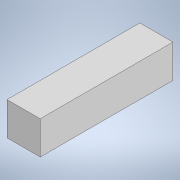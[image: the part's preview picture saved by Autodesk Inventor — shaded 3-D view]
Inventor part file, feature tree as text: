
AUTODESK INVENTOR PART (.ipt)
format: ipt  version: 2022 (Build 260153000, 153)  size: 90,112 bytes
history: native  units: mm
features: extrude x1, sketch x1
ambient origin geometry x8: Origin, YZ Plane, XZ Plane, XY Plane, X Axis, Y Axis, Z Axis, Center Point
bodies: Solid1 (feature_tree)
feature tree (2):
  extrude  "Extrusion1"  Depth=5.0mm
  sketch  "Sketch1"  dims[d0=5.0mm d1=5.0mm d2=20.0mm d3=0.0mm]
